SOLIDWORKS PART (.sldprt)
format: sldprt  version: not decoded by parser v0  size: 258,560 bytes
history: native  units: mm
features: sketch x14, cut_extrude x8, extrude x6, fillet x3 + 2 further entries (+8 scaffold rows collapsed; 3 parser-record rows omitted)
feature tree (44):
  scaffold x8  (default folders/planes/origin — collapsed)
  parser-record x3  (decoder bookkeeping rows leaked as tree rows — omitted from the tree; the rows remain in map.json)
  "ID2"
  "ID3"
  sketch  "Sketch1"  dims[D1=5.334mm D2=28.575mm]
  extrude  "Base-Extrude"  Depth=63.5mm
  sketch  "Sketch2"  dims[D1=18.034mm]
  extrude  "Boss-Extrude1"  [1 undecoded]
  sketch  "Sketch3"  dims[D1=7.62mm]
  cut_extrude  "Cut-Extrude1"  [1 undecoded]
  sketch  "Sketch5"  dims[D1=16.51mm D2=~20.914707mm]
  cut_extrude  "Cut-Extrude3"  [1 undecoded]
  sketch  "Sketch6"  dims[D1=16.51mm]
  cut_extrude  "Cut-Extrude4"  [1 undecoded]
  sketch  "Sketch8"  dims[D1=4.191mm]
  extrude  "Boss-Extrude2"  [1 undecoded]
  sketch  "Sketch9"  dims[D1=1.5748mm D2=3.175mm]
  extrude  "Boss-Extrude3"  Depth=24.638mm
  fillet  "Fillet1"  Radius=3.175mm
  fillet  "Fillet2"  Radius=3.175mm
  sketch  "Sketch10"  dims[D1=1.5748mm]
  extrude  "Boss-Extrude5"  Depth=3.81mm
  sketch  "Sketch11"
  cut_extrude  "Cut-Extrude5"  [1 undecoded]
  sketch  "Sketch12"  dims[D1=1.5748mm]
  extrude  "Boss-Extrude6"  [1 undecoded]
  sketch  "Sketch13"
  cut_extrude  "Cut-Extrude6"  [1 undecoded]
  sketch  "Sketch14"  dims[D1=~7.23161mm]
  cut_extrude  "Cut-Extrude7"  [1 undecoded]
  sketch  "Sketch15"  dims[D1=8.3312mm]
  cut_extrude  "Cut-Extrude8"  [1 undecoded]
  sketch  "Sketch16"  dims[D1=8.3312mm]
  cut_extrude  "Cut-Extrude9"  [1 undecoded]
  fillet  "Fillet3"  Radius=3.175mm
decode coverage: 18 of 31 modeling features carry decoded parameters; 2 rows unclassified (native names shown)
note: ~ marks probable driven/reference dimensions
note: 11 parameter values undecoded
summary: no parameter record found for 11 features
note: suppression state not decoded; provenance and decode notes live in map.json
